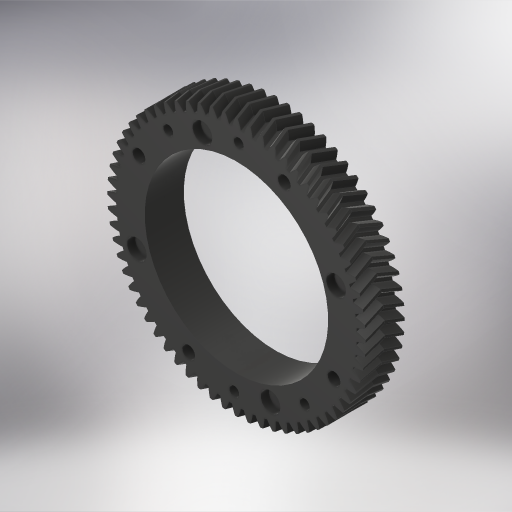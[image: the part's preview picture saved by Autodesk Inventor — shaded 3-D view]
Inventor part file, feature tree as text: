
AUTODESK INVENTOR PART (.ipt)
format: ipt  version: 2023.4 (Build 274418000, 418)  size: 1,580,544 bytes
history: native  units: in
note: dims shown in document units (in); Inventor stores cm internally (conversion verified against a paired STEP export)
features: sketch x4, hole x3, other x2, extrude x1
ambient origin geometry x8: Origin, YZ Plane, XZ Plane, XY Plane, X Axis, Y Axis, Z Axis, Center Point
bodies: Solid1 (feature_tree)
feature tree (10):
  other  "Helical 2M 64T"
  sketch  "Sketch1"  dims[d0=4.7244in d1=3.7in]
  extrude  "Extrusion1"  Depth=3.7in
  other  "DIAMETRIC PITCH"
  hole  "Hole5"  [1 undecoded]
  hole  "Hole6"  [1 undecoded]
  hole  "Hole7"  [1 undecoded]
  sketch  "Sketch7"  dims[d12=1.0in d13=0.0in d14=5.0394in]
  sketch  "Sketch8"  dims[d25=2.1875in d51=4.375in]
  sketch  "Sketch9"  dims[d54=0.75in d55=0.75in d56=0.201in d57=0.5in d58=0.119in d59=0.25in d60=0.5635in d61=1.0in d62=0.0in d64=1.5748in d66=360.0deg d68=0.26in d69=0.75in d70=0.375in d71=0.25in d72=0.5635in d73=1.0in d74=0.0in d75=1.5748in d77=360.0deg d79=4.24in d80=45.0deg d81=1.5748in d83=360.0deg d85=0.4in d86=0.75in d87=0.375in d88=0.25in d89=0.5635in d90=0.17in d91=0.0in]
note: 3 required parameter values undecoded (feature->parameter linkage not recoverable at this tier; creation-order binding heuristic only, values carry confidence <= 0.55)
